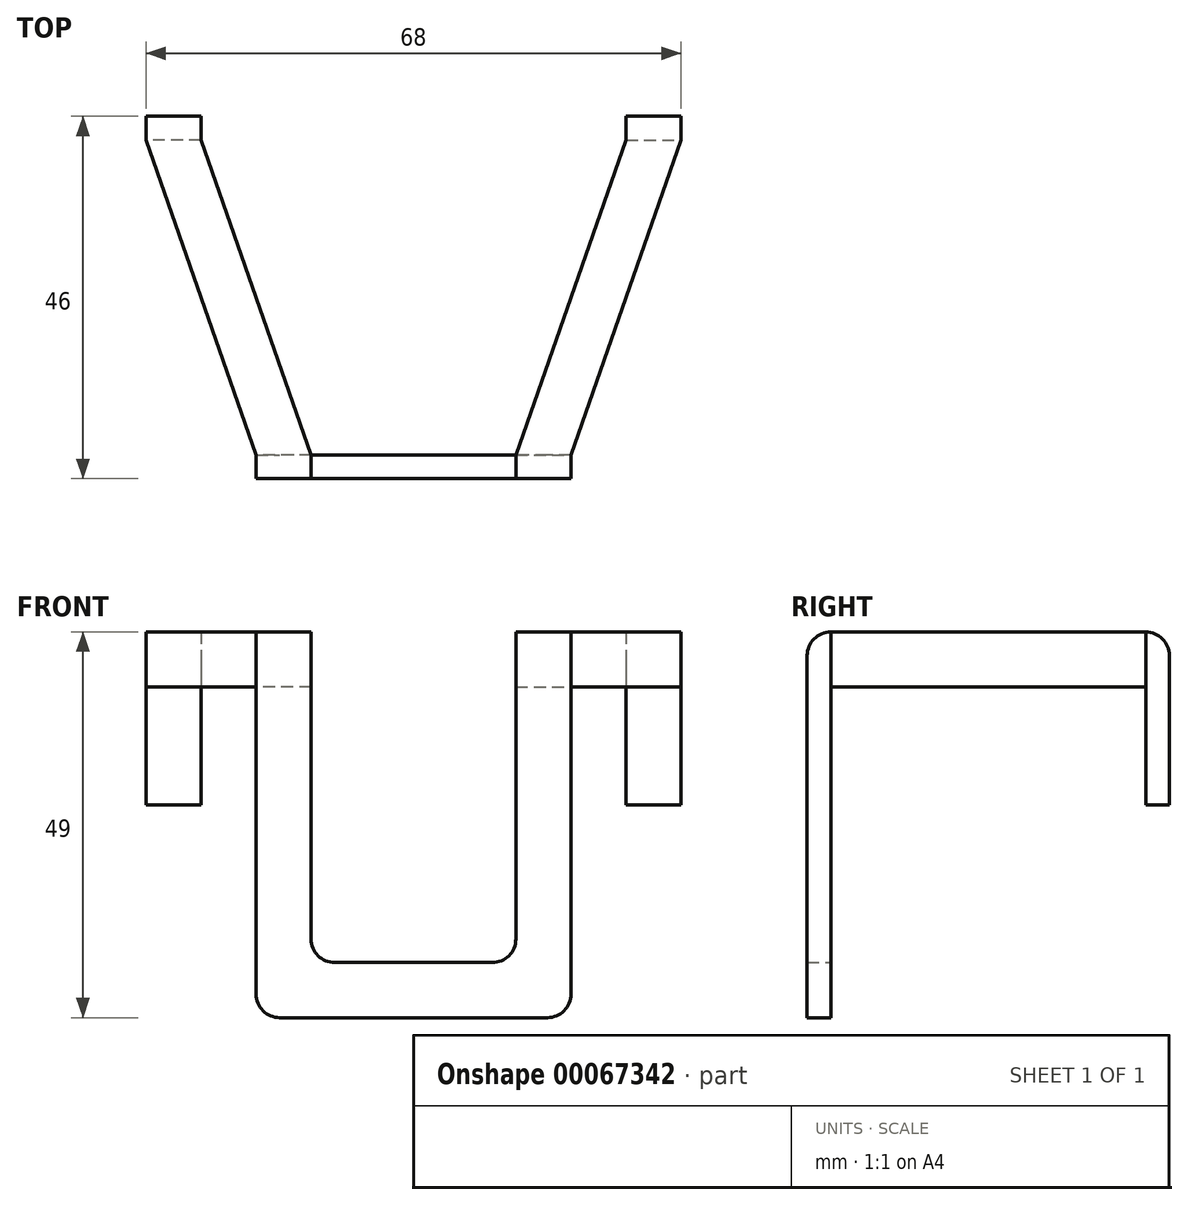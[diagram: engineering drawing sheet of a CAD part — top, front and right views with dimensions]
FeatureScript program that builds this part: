
annotation { "Feature Type Name" : "Feature", "Feature Type Description" : "" }
export const myFeature = defineFeature(function(context is Context, id is Id, definition is map)
    precondition{}
    {
        {
            var Q0;
            Q0=qCreatedBy(makeId("Front.planeOp"),FACE);
            var sketch = newSketch(context, id + "F0", { "sketchPlane" : qUnion([Q0])});
            skLineSegment(sketch, "E0", {"start": v(-20, 49) * mm, "end": v(-20, 0) * mm});
            skLineSegment(sketch, "E1", {"start": v(-13, 7) * mm, "end": v(-13, 49) * mm});
            skLineSegment(sketch, "E2", {"start": v(-13, 49) * mm, "end": v(-20, 49) * mm});
            skLineSegment(sketch, "E3", {"start": v(-13, 7) * mm, "end": v(0, 7) * mm});
            skLineSegment(sketch, "E4", {"start": v(0, 7) * mm, "end": v(0, 0) * mm});
            skLineSegment(sketch, "E5", {"start": v(0, 0) * mm, "end": v(-20, 0) * mm});
            skSolve(sketch);
        }
        {
            var Q0;
            Q0 = qSketchRegion(id + "F0", true);
            extrude(context, id + "F1", {"entities" : qUnion([Q0]), "depth" : 3 * mm});
        }
        {
            var Q0;
            Q0=makeQuery(id+"F1.opExtrude","CAP_FACE",FACE,{"disambiguationData":[OSD([sQuery(id+"F0.wireOp",EDGE,"E0"),sQuery(id+"F0.wireOp",EDGE,"59hPTzeE-vCNL-50nT-LDFU-T32IQ8UCFiRx"),sQuery(id+"F0.wireOp",EDGE,"8YtFZzTf-jURS-QAxp-U71V-Ws7yrMMDVjRU"),sQuery(id+"F0.wireOp",EDGE,"zKKIdWAI-MQpJ-4Xrx-4W18-nBhanUHwFPXB"),sQuery(id+"F0.wireOp",EDGE,"ySnqT2Ln-2shq-C34v-Eb41-mcF3oL4ltvz9"),sQuery(id+"F0.wireOp",EDGE,"mPaNVMRv-eZLk-giN9-V3yt-aZmEMu62LK7H"),sQuery(id+"F0.wireOp",EDGE,"E1"),sQuery(id+"F0.wireOp",EDGE,"E2")])],"isStart":true});
            var sketch = newSketch(context, id + "F2", { "sketchPlane" : qUnion([Q0])});
            skLineSegment(sketch, "E6.bottom", {"start": v(13, 49) * mm, "end": v(20, 49) * mm});
            skLineSegment(sketch, "E6.top", {"start": v(13, 42) * mm, "end": v(20, 42) * mm});
            skLineSegment(sketch, "E6.left", {"start": v(13, 49) * mm, "end": v(13, 42) * mm});
            skLineSegment(sketch, "E6.right", {"start": v(20, 49) * mm, "end": v(20, 42) * mm});
            skSolve(sketch);
        }
        {
            var Q0;
            {var subQ5=sQuery(id+"F2.wireOp",EDGE,"E6.top");Q0=makeQuery(id+"F2.imprint","IMPRINT",FACE,{"disambiguationData":[TD([[makeQuery(id+"F2.imprint","IMPRINT",EDGE,{"derivedFrom":subQ5}),-1.0]])]});}
            cPlane(context, id + "F3", {"entities" : qUnion([Q0]), "cplaneType" : CPlaneType.OFFSET, "offset" : 40 * mm, "width" : 150 * mm, "height" : 150 * mm});
        }
        {
            var Q0;
            Q0=qCreatedBy(id+"F3.planeOp",FACE);
            var sketch = newSketch(context, id + "F4", { "sketchPlane" : qUnion([Q0])});
            skLineSegment(sketch, "E7.bottom", {"start": v(27, 49) * mm, "end": v(34, 49) * mm});
            skLineSegment(sketch, "E7.top", {"start": v(27, 42) * mm, "end": v(34, 42) * mm});
            skLineSegment(sketch, "E7.left", {"start": v(27, 49) * mm, "end": v(27, 42) * mm});
            skLineSegment(sketch, "E7.right", {"start": v(34, 49) * mm, "end": v(34, 42) * mm});
            skSolve(sketch);
        }
        {
            var Q1;
            Q1=makeQuery(id+"F2.imprint","IMPRINT",FACE,{"disambiguationData":[TD([[makeQuery(id+"F2.imprint","IMPRINT",EDGE,{"derivedFrom":sQuery(id+"F2.wireOp",EDGE,"E6.bottom")}),-1.0]])]});
            var Q2;
            Q2=makeQuery(id+"F4.imprint","IMPRINT",FACE,{"disambiguationData":[TD([[makeQuery(id+"F4.imprint","IMPRINT",EDGE,{"derivedFrom":sQuery(id+"F4.wireOp",EDGE,"E7.bottom")}),-1.0]])]});
            loft(context, id + "F5", {"operationType" : NewBodyOperationType.ADD, "sheetProfilesArray" : [{ "sheetProfileEntities" : qUnion([Q1]) }, { "sheetProfileEntities" : qUnion([Q2]) }]});
        }
        {
            var Q0;
            Q0=makeQuery(id+"F5.opLoft","CAP_FACE",FACE,{"disambiguationData":[OSD([makeQuery(id+"F4.imprint","IMPRINT",FACE,{"disambiguationData":[TD([[makeQuery(id+"F4.imprint","IMPRINT",EDGE,{"derivedFrom":sQuery(id+"F4.wireOp",EDGE,"E7.bottom")}),-1.0]])]})])],"isStart":true});
            var sketch = newSketch(context, id + "F6", { "sketchPlane" : qUnion([Q0])});
            skLineSegment(sketch, "E8.bottom", {"start": v(34, 49) * mm, "end": v(27, 49) * mm});
            skLineSegment(sketch, "E8.top", {"start": v(34, 27) * mm, "end": v(27, 27) * mm});
            skLineSegment(sketch, "E8.left", {"start": v(34, 49) * mm, "end": v(34, 27) * mm});
            skLineSegment(sketch, "E8.right", {"start": v(27, 49) * mm, "end": v(27, 27) * mm});
            skSolve(sketch);
        }
        {
            var Q0;
            Q0 = qSketchRegion(id + "F6", true);
            extrude(context, id + "F7", {"entities" : qUnion([Q0]), "operationType" : NewBodyOperationType.ADD, "depth" : 3 * mm});
        }
        {
            var Q0;
            Q0=makeQuery(id+"F1.opExtrude","SWEPT_EDGE",EDGE,{"disambiguationData":[OSD([sQuery(id+"F0.wireOp",EDGE,"E1"),sQuery(id+"F0.wireOp",EDGE,"E3")])]});
            var Q1;
            Q1=makeQuery(id+"F1.opExtrude","SWEPT_EDGE",EDGE,{"disambiguationData":[OSD([sQuery(id+"F0.wireOp",EDGE,"E0"),sQuery(id+"F0.wireOp",EDGE,"E5")])]});
            var Q2;
            Q2=makeQuery(id+"F1.opExtrude","CAP_EDGE",EDGE,{"disambiguationData":[OSD([sQuery(id+"F0.wireOp",EDGE,"E2")])],"isStart":false});
            var Q3;
            Q3=makeQuery(id+"F5.opLoft","MID_CAP_EDGE",EDGE,{"disambiguationData":[OSD([sQuery(id+"F0.wireOp",EDGE,"E0"),sQuery(id+"F0.wireOp",EDGE,"E1"),sQuery(id+"F2.wireOp",EDGE,"E6.top"),sQuery(id+"F2.wireOp",EDGE,"E6.left"),sQuery(id+"F2.wireOp",EDGE,"E6.right")])],"capPos":0.0});
            var Q4;
            Q4=makeQuery(id+"F5.opLoft","MID_CAP_EDGE",EDGE,{"disambiguationData":[OSD([sQuery(id+"F4.wireOp",EDGE,"E7.top"),sQuery(id+"F4.wireOp",EDGE,"E7.left"),sQuery(id+"F4.wireOp",EDGE,"E7.right")])],"capPos":1.0});
            var Q5;
            Q5=makeQuery(id+"F7.opExtrude","CAP_EDGE",EDGE,{"disambiguationData":[OSD([sQuery(id+"F6.wireOp",EDGE,"E8.bottom")])],"isStart":false});
            fillet(context, id + "F8", {"entities" : qUnion([Q0, Q1, Q2, Q3, Q4, Q5]), "radius" : 3 * mm, "tangentPropagation" : true, "allowEdgeOverflow" : false});
        }
        {
            var Q0;
            Q0=makeQuery(id+"F1.opExtrude","SWEPT_BODY",BODY,{"disambiguationData":[OSD([sQuery(id+"F0.wireOp",EDGE,"E0"),sQuery(id+"F0.wireOp",EDGE,"E1"),sQuery(id+"F0.wireOp",EDGE,"E2"),sQuery(id+"F0.wireOp",EDGE,"E3"),sQuery(id+"F0.wireOp",EDGE,"E4"),sQuery(id+"F0.wireOp",EDGE,"E5")])]});
            var Q1;
            Q1=qCreatedBy(makeId("Right.planeOp"),FACE);
            mirror(context, id + "F9", {"operationType" : NewBodyOperationType.ADD, "entities" : qUnion([Q0]), "mirrorPlane" : qUnion([Q1])});
        }
    });
